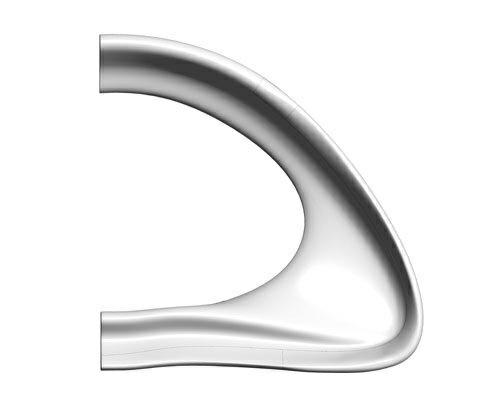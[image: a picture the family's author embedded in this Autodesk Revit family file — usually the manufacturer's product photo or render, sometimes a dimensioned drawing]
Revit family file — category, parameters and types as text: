
# Revit family: CITY ALPHABET litera „V” poziomo_1
name_source: partatom
category: Meble
revit_build: Autodesk Revit 2018 (Build: 20190510_1515(x64)
units: mm (PartAtom-declared; Revit-internal decimal feet)

## family parameters
Numer OmniClass = 23.40.10.11.14
Obiekt nadrzędny = Powierzchnia
Punkt obliczania pomieszczeń = Nie
Tnij formami wycięć po wczytaniu = Nie
Tytuł OmniClass = Exterior Seating
Współdzielony = Nie

## types (1)
- CITY ALPHABET litera „V”
    Domyślna rzędna = 1219 mm
    Długość = 1850 mm  [stored 6.06955 ft]
    IfcExportAs = IfcFurnishingElement
    Komentarze do typu = Ławka
    Materiał - informacja = Szeroki wybór kolorów wg palety RAL. Istnieje również możliwość specjalnego wykonania
kolorystycznego na indywidualne zapytanie klienta.
    Model = CITY ALPHABET litera „V”
    Obraz typu = V.jpg
    Producent = Astrini Design
    Szerokość = 1900 mm  [stored 6.2336 ft]
    Temepratura użytkowania = -40°C do 80°C, ( -40°F do 176°F )
    URL = http://astrini-design.pl
    Waga (szacunkowo) = 80.00 kg
    Waga po wypełnieniu (szacunkowo) = 130.00 kg
    Wysokość = 850 mm  [stored 2.78871 ft]

note: [stored X ft] marks values corroborated as IEEE doubles in the binary element streams (Revit-internal decimal feet)
